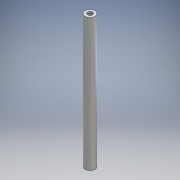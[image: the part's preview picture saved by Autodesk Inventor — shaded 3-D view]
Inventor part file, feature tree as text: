
AUTODESK INVENTOR PART (.ipt)
format: ipt  version: 2016 (Build 200138000, 138)  size: 101,376 bytes
history: native  units: mm
features: sketch x2, extrude x2, hole x2, other x1
ambient origin geometry x8: Origin, YZ Plane, XZ Plane, XY Plane, X Axis, Y Axis, Z Axis, Center Point
bodies: Body1 (feature_tree)
feature tree (7):
  other  "ソリッド1"
  sketch  "スケッチ1"
  extrude  "押し出し1"  Depth=6.0mm
  sketch  "スケッチ2"
  extrude  "押し出し2"  Depth=3.001mm
  hole  "穴1"  [1 undecoded]
  hole  "穴2"  [1 undecoded]
note: 2 required parameter values undecoded (feature->parameter linkage not recoverable at this tier; creation-order binding heuristic only, values carry confidence <= 0.55)
